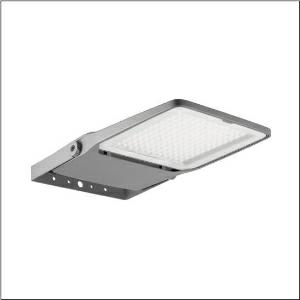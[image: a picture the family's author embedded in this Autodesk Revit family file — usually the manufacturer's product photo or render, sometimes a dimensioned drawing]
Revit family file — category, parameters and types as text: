
# Revit family: floodlight_fl_20_midi___pl61_5xa7682e3c2ac_2046
name_source: partatom
category: Lighting Fixtures
units: mm (PartAtom-declared; Revit-internal decimal feet)

## family parameters
Cut with Voids When Loaded = No
Host = Face
Light Source = No
Part Type = Normal
Room Calculation Point = No
Round Connector Dimension = Use Diameter
Shared = No

## types (1)
- --- (1 x LED 5000K / CRI = 70 (unbekannt), 27570 lm, 5000K)
    Apparent Load = 208 VA
    CIE Flux Codes = 33 65 98 100 100
    Color Rendering = 70
    Color Temperature = 5000K
    Default Elevation = 1800 mm
    Description = Floodlight FL 20 midi, floodlight, primary light control with lens, of plastic, primary optical cover: protective disc, of toughened safety glass, transparent, light distribution: PL61, light emission: direct distribution, primary light characteristic: asymmetric, installation type: surface-mounted, LED High Power LED, rated luminous flux: 27.570 lm, light colour: 750, colour temperature: 5000K, control gear: ECG Plus, control: flexible luminous flux parameterisation, time-dependent luminous flux control, digital communication interface, power reduction, overheat protection, electronic power reduction, with terminal, 5-pole, max. 2.5mm², mains connection: 220..240V, AC, 50/60Hz, rated input power: 208W, LED unit, of diecast aluminium, powder-coated, Siteco® metallic grey (DB 702S), length: 731 mm, width: 450 mm, height: 76mm, housing frame, of diecast aluminium, powder-coated, Siteco® metallic grey (DB 702S), wall fastening, of steel, powder-coated, Siteco® metallic grey (DB 702S), DALIprotection rating (complete): IP66, insulation class (complete): insulation class II (safety insulation), certification: CE, ENEC, VDE, protection symbol: D, permissible ambient temperature for indoor applications: -40..+40°C, permissible ambient temperature for outdoor applications: -40..+50°C, standard: DIN EN 12944, packaging unit: 1 piece

Light Distribution: PL61
    Height = 76 mm
    Lamp = 1 x LED 5000K / CRI >= 70 (unbekannt)
    Lamp Light Flux = 27570 lm
    Lamp count = 1
    Length = 731 mm
    Luminous efficacy = 133 lm/W
    Manufacturer = Siteco
    ModVariant = No
    Model = 5XA7682E3C2AC
    Number of Poles = 1
    OnlyDefault = Yes
    Power Factor = 1
    Product Name = Floodlight FL 20 midi | PL61
    Product group = floodlight | pylon top
    ProductGroupID = 6101
    Protection Class = Protection class II
    Protection Degree = IP 66
    RLX_Detail_Level = 1
    RlxData = <blob elided: 92233 chars, md5=5b75fd7b>
    Socket = socket
    Standby Power = 0 W
    System Light Flux = 27570 lm
    System Power = 208 W
    Type Comments = factory setting: luminous flux: 100 % | dim-lin: 254 | 484 mA
    Type Image = l_1005944.jpg
    URL = http://relux.com
    VarID = @adj_142173
    Voltage = 0 V
    Weight = 0.00 kg
    Width = 450 mm

## geometry (parser evidence)
native form markers: Blend x4, Sweep x14
no freeform markers — native parametric forms only
